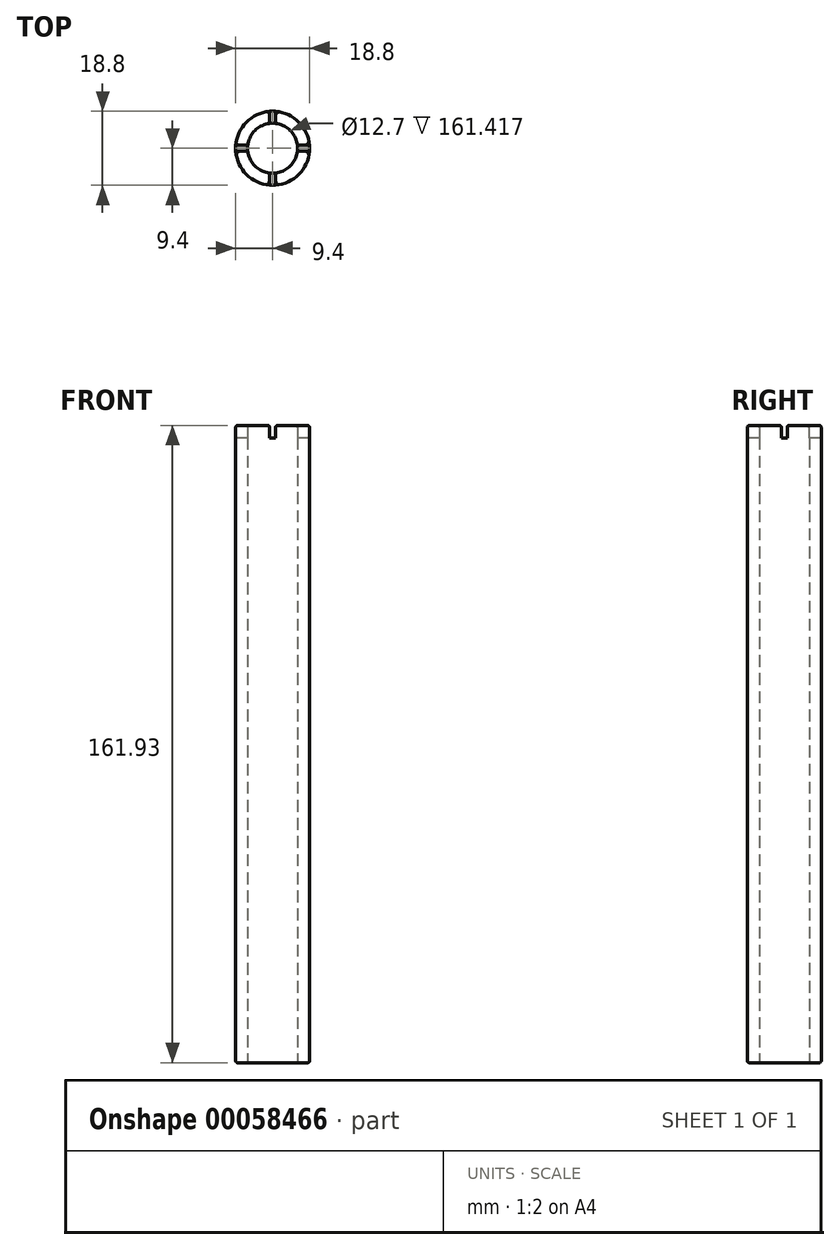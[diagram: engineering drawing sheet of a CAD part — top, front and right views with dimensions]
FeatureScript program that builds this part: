
annotation { "Feature Type Name" : "Feature", "Feature Type Description" : "" }
export const myFeature = defineFeature(function(context is Context, id is Id, definition is map)
    precondition{}
    {
        {
            var Q0;
            Q0=qCreatedBy(makeId("Top.planeOp"),FACE);
            var sketch = newSketch(context, id + "F0", { "sketchPlane" : qUnion([Q0])});
            skCircle(sketch, "E0", {"center": v(0, 0) * mm, "radius": 6.35 * mm});
            skCircle(sketch, "E1", {"center": v(0, 0) * mm, "radius": 9.4 * mm});
            skSolve(sketch);
        }
        {
            var Q0;
            Q0=makeQuery(id+"F0.imprint","IMPRINT",FACE,{"disambiguationData":[TD([[makeQuery(id+"F0.imprint","IMPRINT",EDGE,{"derivedFrom":sQuery(id+"F0.wireOp",EDGE,"E0")}),-1.0]])]});
            extrude(context, id + "F1", {"entities" : qUnion([Q0]), "depth" : 158.75 * mm});
        }
        {
            var Q0;
            Q0=makeQuery(id+"F1.opExtrude","CAP_FACE",FACE,{"disambiguationData":[OSD([sQuery(id+"F0.wireOp",EDGE,"E0"),sQuery(id+"F0.wireOp",EDGE,"E1")])],"isStart":false});
            var sketch = newSketch(context, id + "F2", { "sketchPlane" : qUnion([Q0])});
            skLineSegment(sketch, "E2.rect.bottom", {"start": v(9.77, 0.76) * mm, "end": v(-9.77, 0.76) * mm});
            skLineSegment(sketch, "E2.rect.top", {"start": v(9.77, -0.76) * mm, "end": v(-9.77, -0.76) * mm});
            skLineSegment(sketch, "E2.rect.left", {"start": v(9.77, 0.76) * mm, "end": v(9.77, -0.76) * mm});
            skLineSegment(sketch, "E2.rect.right", {"start": v(-9.77, 0.76) * mm, "end": v(-9.77, -0.76) * mm});
            skPoint(sketch, "E2.rect.middle", {"position": v(0, 0) * mm});
            skLineSegment(sketch, "E3.rect.bottom", {"start": v(0.76, 9.74) * mm, "end": v(-0.76, 9.74) * mm});
            skLineSegment(sketch, "E3.rect.top", {"start": v(0.76, -9.74) * mm, "end": v(-0.76, -9.74) * mm});
            skLineSegment(sketch, "E3.rect.left", {"start": v(0.76, 9.74) * mm, "end": v(0.76, -9.74) * mm});
            skLineSegment(sketch, "E3.rect.right", {"start": v(-0.76, 9.74) * mm, "end": v(-0.76, -9.74) * mm});
            skSolve(sketch);
        }
        {
            var Q0;
            {var subQ0=sQuery(id+"F2.wireOp",EDGE,"E2.rect.bottom");var subQ1=makeQuery(id+"F1.opExtrude","CAP_EDGE",EDGE,{"disambiguationData":[OSD([sQuery(id+"F0.wireOp",EDGE,"E1")])],"isStart":false});var subQ2=makeQuery(id+"F2.imprint","INTERSECT",VERTEX,{"disambiguationData":[OD(1.0)],"derivedFrom":[subQ1,subQ0]});Q0=makeQuery(id+"F2.imprint","IMPRINT",FACE,{"disambiguationData":[TD([[makeQuery(id+"F2.imprint","IMPRINT",EDGE,{"disambiguationData":[TD([[subQ2,1.0]])],"derivedFrom":subQ0}),-1.0]])]});}
            var Q1;
            {var subQ0=sQuery(id+"F2.wireOp",EDGE,"E2.rect.bottom");var subQ1=makeQuery(id+"F1.opExtrude","CAP_EDGE",EDGE,{"disambiguationData":[OSD([sQuery(id+"F0.wireOp",EDGE,"E1")])],"isStart":false});var subQ2=makeQuery(id+"F2.imprint","INTERSECT",VERTEX,{"disambiguationData":[OD(0.0)],"derivedFrom":[subQ1,subQ0]});Q1=makeQuery(id+"F2.imprint","IMPRINT",FACE,{"disambiguationData":[TD([[makeQuery(id+"F2.imprint","IMPRINT",EDGE,{"disambiguationData":[TD([[subQ2,-1.0]])],"derivedFrom":subQ0}),-1.0]])]});}
            var Q2;
            {var subQ0=sQuery(id+"F2.wireOp",EDGE,"E2.rect.top");var subQ1=makeQuery(id+"F1.opExtrude","CAP_EDGE",EDGE,{"disambiguationData":[OSD([sQuery(id+"F0.wireOp",EDGE,"E1")])],"isStart":false});var subQ2=makeQuery(id+"F2.imprint","INTERSECT",VERTEX,{"disambiguationData":[OD(0.0)],"derivedFrom":[subQ1,subQ0]});Q2=makeQuery(id+"F2.imprint","IMPRINT",FACE,{"disambiguationData":[TD([[makeQuery(id+"F2.imprint","IMPRINT",EDGE,{"disambiguationData":[TD([[subQ2,-1.0]])],"derivedFrom":subQ0}),1.0]])]});}
            var Q3;
            {var subQ0=sQuery(id+"F2.wireOp",EDGE,"E2.rect.top");var subQ1=makeQuery(id+"F1.opExtrude","CAP_EDGE",EDGE,{"disambiguationData":[OSD([sQuery(id+"F0.wireOp",EDGE,"E1")])],"isStart":false});var subQ2=makeQuery(id+"F2.imprint","INTERSECT",VERTEX,{"disambiguationData":[OD(1.0)],"derivedFrom":[subQ1,subQ0]});Q3=makeQuery(id+"F2.imprint","IMPRINT",FACE,{"disambiguationData":[TD([[makeQuery(id+"F2.imprint","IMPRINT",EDGE,{"disambiguationData":[TD([[subQ2,1.0]])],"derivedFrom":subQ0}),1.0]])]});}
            extrude(context, id + "F3", {"entities" : qUnion([Q0, Q1, Q2, Q3]), "operationType" : NewBodyOperationType.ADD, "depth" : 3.17 * mm});
        }
        {
            var Q0;
            {var subQ0=sQuery(id+"F2.wireOp",EDGE,"E3.rect.right");Q0=makeQuery(id+"F3.opExtrude","CAP_EDGE",EDGE,{"disambiguationData":[OSD([subQ0]),TDD([makeQuery(id+"F2.imprint","IMPRINT",EDGE,{"disambiguationData":[TD([[makeQuery(id+"F2.imprint","INTERSECT",VERTEX,{"disambiguationData":[OD(0.0)],"derivedFrom":[makeQuery(id+"F1.opExtrude","CAP_EDGE",EDGE,{"disambiguationData":[OSD([sQuery(id+"F0.wireOp",EDGE,"E1")])],"isStart":false}),subQ0]}),-1.0]])],"derivedFrom":subQ0})])],"isStart":false});}
            var Q1;
            {var subQ0=sQuery(id+"F2.wireOp",EDGE,"E3.rect.left");Q1=makeQuery(id+"F3.opExtrude","CAP_EDGE",EDGE,{"disambiguationData":[OSD([subQ0]),TDD([makeQuery(id+"F2.imprint","IMPRINT",EDGE,{"disambiguationData":[TD([[makeQuery(id+"F2.imprint","INTERSECT",VERTEX,{"disambiguationData":[OD(0.0)],"derivedFrom":[makeQuery(id+"F1.opExtrude","CAP_EDGE",EDGE,{"disambiguationData":[OSD([sQuery(id+"F0.wireOp",EDGE,"E1")])],"isStart":false}),subQ0]}),-1.0]])],"derivedFrom":subQ0})])],"isStart":false});}
            var Q2;
            {var subQ0=sQuery(id+"F2.wireOp",EDGE,"E2.rect.bottom");Q2=makeQuery(id+"F3.opExtrude","CAP_EDGE",EDGE,{"disambiguationData":[OSD([subQ0]),TDD([makeQuery(id+"F2.imprint","IMPRINT",EDGE,{"disambiguationData":[TD([[makeQuery(id+"F2.imprint","INTERSECT",VERTEX,{"disambiguationData":[OD(0.0)],"derivedFrom":[makeQuery(id+"F1.opExtrude","CAP_EDGE",EDGE,{"disambiguationData":[OSD([sQuery(id+"F0.wireOp",EDGE,"E1")])],"isStart":false}),subQ0]}),-1.0]])],"derivedFrom":subQ0})])],"isStart":false});}
            var Q3;
            {var subQ0=sQuery(id+"F2.wireOp",EDGE,"E2.rect.top");Q3=makeQuery(id+"F3.opExtrude","CAP_EDGE",EDGE,{"disambiguationData":[OSD([subQ0]),TDD([makeQuery(id+"F2.imprint","IMPRINT",EDGE,{"disambiguationData":[TD([[makeQuery(id+"F2.imprint","INTERSECT",VERTEX,{"disambiguationData":[OD(0.0)],"derivedFrom":[makeQuery(id+"F1.opExtrude","CAP_EDGE",EDGE,{"disambiguationData":[OSD([sQuery(id+"F0.wireOp",EDGE,"E1")])],"isStart":false}),subQ0]}),-1.0]])],"derivedFrom":subQ0})])],"isStart":false});}
            var Q4;
            {var subQ0=sQuery(id+"F2.wireOp",EDGE,"E3.rect.left");Q4=makeQuery(id+"F3.opExtrude","CAP_EDGE",EDGE,{"disambiguationData":[OSD([subQ0]),TDD([makeQuery(id+"F2.imprint","IMPRINT",EDGE,{"disambiguationData":[TD([[makeQuery(id+"F2.imprint","INTERSECT",VERTEX,{"disambiguationData":[OD(1.0)],"derivedFrom":[makeQuery(id+"F1.opExtrude","CAP_EDGE",EDGE,{"disambiguationData":[OSD([sQuery(id+"F0.wireOp",EDGE,"E1")])],"isStart":false}),subQ0]}),1.0]])],"derivedFrom":subQ0})])],"isStart":false});}
            var Q5;
            {var subQ0=sQuery(id+"F2.wireOp",EDGE,"E3.rect.right");Q5=makeQuery(id+"F3.opExtrude","CAP_EDGE",EDGE,{"disambiguationData":[OSD([subQ0]),TDD([makeQuery(id+"F2.imprint","IMPRINT",EDGE,{"disambiguationData":[TD([[makeQuery(id+"F2.imprint","INTERSECT",VERTEX,{"disambiguationData":[OD(1.0)],"derivedFrom":[makeQuery(id+"F1.opExtrude","CAP_EDGE",EDGE,{"disambiguationData":[OSD([sQuery(id+"F0.wireOp",EDGE,"E1")])],"isStart":false}),subQ0]}),1.0]])],"derivedFrom":subQ0})])],"isStart":false});}
            var Q6;
            {var subQ0=sQuery(id+"F2.wireOp",EDGE,"E2.rect.top");Q6=makeQuery(id+"F3.opExtrude","CAP_EDGE",EDGE,{"disambiguationData":[OSD([subQ0]),TDD([makeQuery(id+"F2.imprint","IMPRINT",EDGE,{"disambiguationData":[TD([[makeQuery(id+"F2.imprint","INTERSECT",VERTEX,{"disambiguationData":[OD(1.0)],"derivedFrom":[makeQuery(id+"F1.opExtrude","CAP_EDGE",EDGE,{"disambiguationData":[OSD([sQuery(id+"F0.wireOp",EDGE,"E1")])],"isStart":false}),subQ0]}),1.0]])],"derivedFrom":subQ0})])],"isStart":false});}
            var Q7;
            {var subQ0=sQuery(id+"F2.wireOp",EDGE,"E2.rect.bottom");Q7=makeQuery(id+"F3.opExtrude","CAP_EDGE",EDGE,{"disambiguationData":[OSD([subQ0]),TDD([makeQuery(id+"F2.imprint","IMPRINT",EDGE,{"disambiguationData":[TD([[makeQuery(id+"F2.imprint","INTERSECT",VERTEX,{"disambiguationData":[OD(1.0)],"derivedFrom":[makeQuery(id+"F1.opExtrude","CAP_EDGE",EDGE,{"disambiguationData":[OSD([sQuery(id+"F0.wireOp",EDGE,"E1")])],"isStart":false}),subQ0]}),1.0]])],"derivedFrom":subQ0})])],"isStart":false});}
            var Q8;
            {var subQ0=sQuery(id+"F0.wireOp",EDGE,"E1");var subQ1=makeQuery(id+"F1.opExtrude","CAP_EDGE",EDGE,{"disambiguationData":[OSD([subQ0])],"isStart":false});Q8=makeQuery(id+"F3.opExtrude","CAP_EDGE",EDGE,{"disambiguationData":[OSD([subQ0]),TDD([makeQuery(id+"F2.imprint","IMPRINT",EDGE,{"disambiguationData":[TD([[makeQuery(id+"F2.imprint","INTERSECT",VERTEX,{"disambiguationData":[OD(1.0)],"derivedFrom":[subQ1,sQuery(id+"F2.wireOp",EDGE,"E2.rect.bottom")]}),1.0]])],"derivedFrom":subQ1})])],"isStart":false});}
            var Q9;
            {var subQ0=sQuery(id+"F0.wireOp",EDGE,"E1");var subQ1=makeQuery(id+"F1.opExtrude","CAP_EDGE",EDGE,{"disambiguationData":[OSD([subQ0])],"isStart":false});Q9=makeQuery(id+"F3.opExtrude","CAP_EDGE",EDGE,{"disambiguationData":[OSD([subQ0]),TDD([makeQuery(id+"F2.imprint","IMPRINT",EDGE,{"disambiguationData":[TD([[makeQuery(id+"F2.imprint","INTERSECT",VERTEX,{"disambiguationData":[OD(0.0)],"derivedFrom":[subQ1,sQuery(id+"F2.wireOp",EDGE,"E2.rect.bottom")]}),-1.0]])],"derivedFrom":subQ1})])],"isStart":false});}
            var Q10;
            {var subQ0=sQuery(id+"F0.wireOp",EDGE,"E1");var subQ1=makeQuery(id+"F1.opExtrude","CAP_EDGE",EDGE,{"disambiguationData":[OSD([subQ0])],"isStart":false});Q10=makeQuery(id+"F3.opExtrude","CAP_EDGE",EDGE,{"disambiguationData":[OSD([subQ0]),TDD([makeQuery(id+"F2.imprint","IMPRINT",EDGE,{"disambiguationData":[TD([[makeQuery(id+"F2.imprint","INTERSECT",VERTEX,{"disambiguationData":[OD(0.0)],"derivedFrom":[subQ1,sQuery(id+"F2.wireOp",EDGE,"E2.rect.top")]}),1.0]])],"derivedFrom":subQ1})])],"isStart":false});}
            var Q11;
            {var subQ0=sQuery(id+"F0.wireOp",EDGE,"E1");var subQ1=makeQuery(id+"F1.opExtrude","CAP_EDGE",EDGE,{"disambiguationData":[OSD([subQ0])],"isStart":false});Q11=makeQuery(id+"F3.opExtrude","CAP_EDGE",EDGE,{"disambiguationData":[OSD([subQ0]),TDD([makeQuery(id+"F2.imprint","IMPRINT",EDGE,{"disambiguationData":[TD([[makeQuery(id+"F2.imprint","INTERSECT",VERTEX,{"disambiguationData":[OD(1.0)],"derivedFrom":[subQ1,sQuery(id+"F2.wireOp",EDGE,"E2.rect.top")]}),-1.0]])],"derivedFrom":subQ1})])],"isStart":false});}
            var Q12;
            {var subQ0=sQuery(id+"F0.wireOp",EDGE,"E0");var subQ1=makeQuery(id+"F1.opExtrude","CAP_EDGE",EDGE,{"disambiguationData":[OSD([subQ0])],"isStart":false});Q12=makeQuery(id+"F3.opExtrude","CAP_EDGE",EDGE,{"disambiguationData":[OSD([subQ0]),TDD([makeQuery(id+"F2.imprint","IMPRINT",EDGE,{"disambiguationData":[TD([[makeQuery(id+"F2.imprint","INTERSECT",VERTEX,{"disambiguationData":[OD(0.0)],"derivedFrom":[subQ1,sQuery(id+"F2.wireOp",EDGE,"E2.rect.bottom")]}),-1.0]])],"derivedFrom":subQ1})])],"isStart":false});}
            var Q13;
            {var subQ0=sQuery(id+"F0.wireOp",EDGE,"E0");var subQ1=makeQuery(id+"F1.opExtrude","CAP_EDGE",EDGE,{"disambiguationData":[OSD([subQ0])],"isStart":false});Q13=makeQuery(id+"F3.opExtrude","CAP_EDGE",EDGE,{"disambiguationData":[OSD([subQ0]),TDD([makeQuery(id+"F2.imprint","IMPRINT",EDGE,{"disambiguationData":[TD([[makeQuery(id+"F2.imprint","INTERSECT",VERTEX,{"disambiguationData":[OD(1.0)],"derivedFrom":[subQ1,sQuery(id+"F2.wireOp",EDGE,"E2.rect.bottom")]}),1.0]])],"derivedFrom":subQ1})])],"isStart":false});}
            var Q14;
            {var subQ0=sQuery(id+"F0.wireOp",EDGE,"E0");var subQ1=makeQuery(id+"F1.opExtrude","CAP_EDGE",EDGE,{"disambiguationData":[OSD([subQ0])],"isStart":false});Q14=makeQuery(id+"F3.opExtrude","CAP_EDGE",EDGE,{"disambiguationData":[OSD([subQ0]),TDD([makeQuery(id+"F2.imprint","IMPRINT",EDGE,{"disambiguationData":[TD([[makeQuery(id+"F2.imprint","INTERSECT",VERTEX,{"disambiguationData":[OD(1.0)],"derivedFrom":[subQ1,sQuery(id+"F2.wireOp",EDGE,"E2.rect.top")]}),-1.0]])],"derivedFrom":subQ1})])],"isStart":false});}
            var Q15;
            {var subQ0=sQuery(id+"F0.wireOp",EDGE,"E0");var subQ1=makeQuery(id+"F1.opExtrude","CAP_EDGE",EDGE,{"disambiguationData":[OSD([subQ0])],"isStart":false});Q15=makeQuery(id+"F3.opExtrude","CAP_EDGE",EDGE,{"disambiguationData":[OSD([subQ0]),TDD([makeQuery(id+"F2.imprint","IMPRINT",EDGE,{"disambiguationData":[TD([[makeQuery(id+"F2.imprint","INTERSECT",VERTEX,{"disambiguationData":[OD(0.0)],"derivedFrom":[subQ1,sQuery(id+"F2.wireOp",EDGE,"E2.rect.top")]}),1.0]])],"derivedFrom":subQ1})])],"isStart":false});}
            fillet(context, id + "F4", {"entities" : qUnion([Q0, Q1, Q2, Q3, Q4, Q5, Q6, Q7, Q8, Q9, Q10, Q11, Q12, Q13, Q14, Q15]), "radius" : 0.5 * mm, "tangentPropagation" : true, "allowEdgeOverflow" : false});
        }
        {
            var Q0;
            Q0=makeQuery(id+"F1.opExtrude","CAP_EDGE",EDGE,{"disambiguationData":[OSD([sQuery(id+"F0.wireOp",EDGE,"E0")])],"isStart":true});
            var Q1;
            Q1=makeQuery(id+"F1.opExtrude","CAP_EDGE",EDGE,{"disambiguationData":[OSD([sQuery(id+"F0.wireOp",EDGE,"E1")])],"isStart":true});
            fillet(context, id + "F5", {"entities" : qUnion([Q0, Q1]), "radius" : 0.5 * mm, "tangentPropagation" : true, "allowEdgeOverflow" : false});
        }
    });
